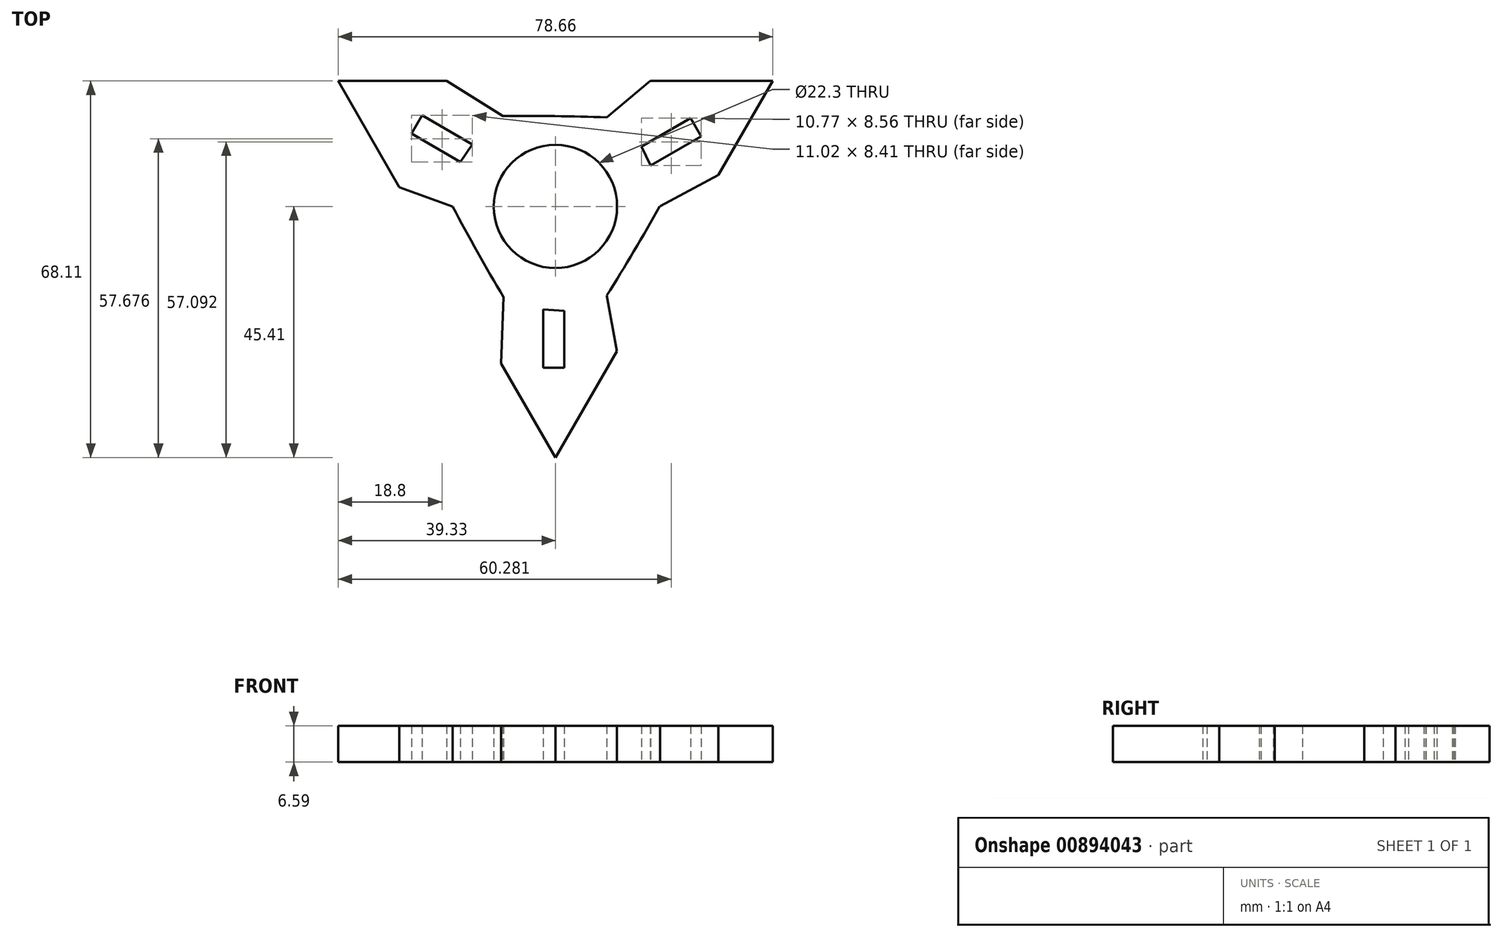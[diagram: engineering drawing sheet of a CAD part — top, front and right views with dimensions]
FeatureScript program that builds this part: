
annotation { "Feature Type Name" : "Feature", "Feature Type Description" : "" }
export const myFeature = defineFeature(function(context is Context, id is Id, definition is map)
    precondition{}
    {
        {
            var Q0;
            Q0=qCreatedBy(makeId("Top.planeOp"),FACE);
            var sketch = newSketch(context, id + "F0", { "sketchPlane" : qUnion([Q0])});
            skCircle(sketch, "E0", {"center": v(0, 0) * mm, "radius": 11.15 * mm});
            skLineSegment(sketch, "E1.1", {"start": v(0, -45.4) * mm, "end": v(11.1, -26.2) * mm});
            skLineSegment(sketch, "E1.2", {"start": v(-9.82, -28.4) * mm, "end": v(0, -45.4) * mm});
            skLineSegment(sketch, "E2.1.0", {"start": v(29.5, 5.69) * mm, "end": v(39.33, 22.7) * mm});
            skLineSegment(sketch, "E2.1.2", {"start": v(39.33, 22.7) * mm, "end": v(17.14, 22.7) * mm});
            skLineSegment(sketch, "E2.2.0", {"start": v(-19.68, 22.7) * mm, "end": v(-39.33, 22.7) * mm});
            skLineSegment(sketch, "E2.2.2", {"start": v(-39.33, 22.7) * mm, "end": v(-28.23, 3.49) * mm});
            skArc(sketch, "E3", {"start": v(-18.6, 0) * mm, "mid": v(-14.1, -8.25) * mm, "end": v(-9.4, -16.4) * mm});
            skArc(sketch, "E4.1.0", {"start": v(9.3, -16.11) * mm, "mid": v(14.2, -8.08) * mm, "end": v(18.9, 0.06) * mm});
            skArc(sketch, "E4.2.0", {"start": v(9.3, 16.11) * mm, "mid": v(-0.1, 16.34) * mm, "end": v(-9.5, 16.33) * mm});
            skLineSegment(sketch, "E5", {"start": v(-19.68, 22.7) * mm, "end": v(-9.5, 16.33) * mm});
            skLineSegment(sketch, "E6", {"start": v(-28.23, 3.49) * mm, "end": v(-18.6, 0) * mm});
            skLineSegment(sketch, "E7.1.2", {"start": v(10.48, -22.72) * mm, "end": v(9.3, -16.11) * mm});
            skLineSegment(sketch, "E7.1.3", {"start": v(-9.82, -28.4) * mm, "end": v(-9.4, -16.4) * mm});
            skLineSegment(sketch, "E7.2.2", {"start": v(17.14, 22.7) * mm, "end": v(9.3, 16.11) * mm});
            skLineSegment(sketch, "E7.2.3", {"start": v(29.5, 5.69) * mm, "end": v(24.49, 3.03) * mm});
            skPoint(sketch, "E8.orphan", {"position": v(18.9, 0.06) * mm});
            skLineSegment(sketch, "E9", {"start": v(24.49, 3.03) * mm, "end": v(18.9, 0.06) * mm});
            skLineSegment(sketch, "E10", {"start": v(10.48, -22.72) * mm, "end": v(11.1, -26.2) * mm});
            skSolve(sketch);
        }
        {
            var Q0;
            Q0 = qSketchRegion(id + "F0", true);
            extrude(context, id + "F1", {"entities" : qUnion([Q0]), "depth" : 6.58 * mm, "offsetDistance" : 25 * mm});
        }
        {
            var Q0;
            Q0=makeQuery(id+"F1.opExtrude","CAP_FACE",FACE,{"disambiguationData":[OSD([sQuery(id+"F0.wireOp",EDGE,"E0"),sQuery(id+"F0.wireOp",EDGE,"E2.2.0"),sQuery(id+"F0.wireOp",EDGE,"E2.2.2"),sQuery(id+"F0.wireOp",EDGE,"E3"),sQuery(id+"F0.wireOp",EDGE,"E4.1.0"),sQuery(id+"F0.wireOp",EDGE,"E4.2.0"),sQuery(id+"F0.wireOp",EDGE,"E5"),sQuery(id+"F0.wireOp",EDGE,"E6"),sQuery(id+"F0.wireOp",EDGE,"E1.2"),sQuery(id+"F0.wireOp",EDGE,"E1.1"),sQuery(id+"F0.wireOp",EDGE,"E7.1.2"),sQuery(id+"F0.wireOp",EDGE,"E7.1.3"),sQuery(id+"F0.wireOp",EDGE,"E2.1.0"),sQuery(id+"F0.wireOp",EDGE,"E2.1.2"),sQuery(id+"F0.wireOp",EDGE,"E7.2.2"),sQuery(id+"F0.wireOp",EDGE,"E7.2.3"),sQuery(id+"F0.wireOp",EDGE,"E9"),sQuery(id+"F0.wireOp",EDGE,"E10")])],"isStart":true});
            var sketch = newSketch(context, id + "F2", { "sketchPlane" : qUnion([Q0])});
            skPoint(sketch, "E11.center", {"position": v(0, 0) * mm});
            skLineSegment(sketch, "E12", {"start": v(-2.2, 18.62) * mm, "end": v(-2.2, 29.14) * mm});
            skLineSegment(sketch, "E13", {"start": v(-2.2, 29.14) * mm, "end": v(1.6, 29.14) * mm});
            skLineSegment(sketch, "E14", {"start": v(1.6, 29.14) * mm, "end": v(1.6, 18.9) * mm});
            skLineSegment(sketch, "E15", {"start": v(1.6, 18.9) * mm, "end": v(-2.2, 18.62) * mm});
            skLineSegment(sketch, "E16.1.0", {"start": v(-15.02, -11.21) * mm, "end": v(-24.13, -16.47) * mm});
            skLineSegment(sketch, "E16.1.1", {"start": v(-26.04, -13.18) * mm, "end": v(-17.18, -8.06) * mm});
            skLineSegment(sketch, "E16.1.2", {"start": v(-24.13, -16.47) * mm, "end": v(-26.04, -13.18) * mm});
            skLineSegment(sketch, "E16.1.3", {"start": v(-17.18, -8.06) * mm, "end": v(-15.02, -11.21) * mm});
            skLineSegment(sketch, "E16.2.0", {"start": v(17.22, -7.4) * mm, "end": v(26.33, -12.66) * mm});
            skLineSegment(sketch, "E16.2.1", {"start": v(24.43, -15.96) * mm, "end": v(15.57, -10.85) * mm});
            skLineSegment(sketch, "E16.2.2", {"start": v(26.33, -12.66) * mm, "end": v(24.43, -15.96) * mm});
            skLineSegment(sketch, "E16.2.3", {"start": v(15.57, -10.85) * mm, "end": v(17.22, -7.4) * mm});
            skSolve(sketch);
        }
        {
            var Q0;
            Q0 = qSketchRegion(id + "F2", true);
            extrude(context, id + "F3", {"entities" : qUnion([Q0]), "operationType" : NewBodyOperationType.REMOVE, "oppositeDirection" : true, "depth" : 25 * mm, "offsetDistance" : 25 * mm});
        }
    });
